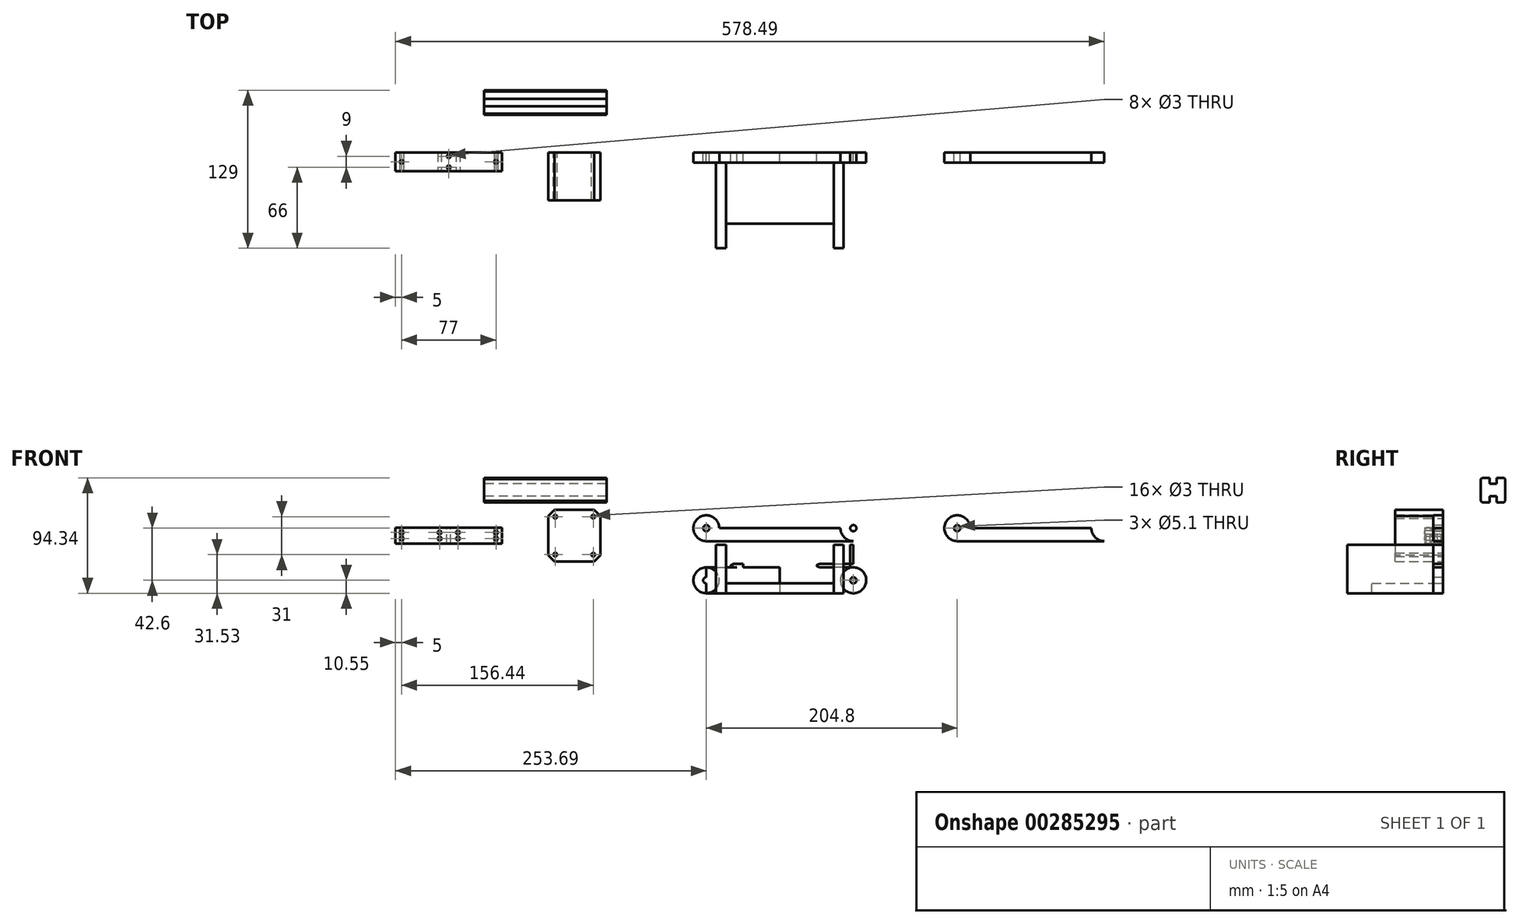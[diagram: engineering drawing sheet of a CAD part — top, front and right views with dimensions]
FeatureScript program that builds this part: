
annotation { "Feature Type Name" : "Feature", "Feature Type Description" : "" }
export const myFeature = defineFeature(function(context is Context, id is Id, definition is map)
    precondition{}
    {
        {
            var Q0;
            Q0=qCreatedBy(makeId("Front.planeOp"),FACE);
            var sketch = newSketch(context, id + "F0", { "sketchPlane" : qUnion([Q0])});
            skLineSegment(sketch, "E0.bottom", {"start": v(-72.24, 27.77) * mm, "end": v(14.76, 27.77) * mm});
            skLineSegment(sketch, "E0.top", {"start": v(-72.24, 14.77) * mm, "end": v(14.76, 14.77) * mm});
            skLineSegment(sketch, "E0.left", {"start": v(-72.24, 27.77) * mm, "end": v(-72.24, 14.77) * mm});
            skLineSegment(sketch, "E0.right", {"start": v(14.76, 27.77) * mm, "end": v(14.76, 14.77) * mm});
            skSolve(sketch);
        }
        {
            var Q0;
            Q0 = qSketchRegion(id + "F0", true);
            extrude(context, id + "F1", {"entities" : qUnion([Q0]), "depth" : 15 * mm, "offsetDistance" : 25 * mm});
        }
        {
            var Q0;
            Q0=makeQuery(id+"F1.opExtrude","CAP_FACE",FACE,{"disambiguationData":[OSD([sQuery(id+"F0.wireOp",EDGE,"E0.bottom"),sQuery(id+"F0.wireOp",EDGE,"E0.top"),sQuery(id+"F0.wireOp",EDGE,"E0.left"),sQuery(id+"F0.wireOp",EDGE,"E0.right")])],"isStart":false});
            var sketch = newSketch(context, id + "F2", { "sketchPlane" : qUnion([Q0])});
            skLineSegment(sketch, "E1.bottom", {"start": v(-72.24, 27.77) * mm, "end": v(14.76, 27.77) * mm});
            skLineSegment(sketch, "E1.top", {"start": v(-72.24, 14.77) * mm, "end": v(14.76, 14.77) * mm});
            skLineSegment(sketch, "E1.left", {"start": v(-72.24, 27.77) * mm, "end": v(-72.24, 14.77) * mm});
            skLineSegment(sketch, "E1.right", {"start": v(14.76, 27.77) * mm, "end": v(14.76, 14.77) * mm});
            skLineSegment(sketch, "E2", {"start": v(-28.74, 27.77) * mm, "end": v(-21.24, 27.77) * mm});
            skLineSegment(sketch, "E3", {"start": v(-21.24, 27.77) * mm, "end": v(-36.24, 27.77) * mm});
            skLineSegment(sketch, "E4", {"start": v(-36.24, 27.77) * mm, "end": v(-67.24, 27.77) * mm});
            skLineSegment(sketch, "E5", {"start": v(-67.24, 27.77) * mm, "end": v(-67.24, 23.77) * mm});
            skLineSegment(sketch, "E6", {"start": v(-67.24, 23.77) * mm, "end": v(-67.24, 18.77) * mm});
            skLineSegment(sketch, "E7", {"start": v(-67.24, 18.77) * mm, "end": v(-67.24, 14.77) * mm});
            skLineSegment(sketch, "E8", {"start": v(-36.24, 27.77) * mm, "end": v(-36.24, 18.77) * mm});
            skLineSegment(sketch, "E9", {"start": v(-36.24, 18.77) * mm, "end": v(-36.24, 23.77) * mm});
            skLineSegment(sketch, "E10", {"start": v(-36.24, 23.77) * mm, "end": v(-21.24, 23.77) * mm});
            skLineSegment(sketch, "E11", {"start": v(-21.24, 23.77) * mm, "end": v(-21.24, 18.77) * mm});
            skLineSegment(sketch, "E12", {"start": v(-21.24, 18.77) * mm, "end": v(9.76, 18.77) * mm});
            skLineSegment(sketch, "E13", {"start": v(9.76, 18.77) * mm, "end": v(9.76, 23.77) * mm});
            skCircle(sketch, "E14", {"center": v(-67.24, 23.77) * mm, "radius": 1.5 * mm});
            skCircle(sketch, "E15", {"center": v(-67.24, 18.77) * mm, "radius": 1.5 * mm});
            skCircle(sketch, "E16", {"center": v(-36.24, 23.77) * mm, "radius": 1.5 * mm});
            skCircle(sketch, "E17", {"center": v(-36.24, 18.77) * mm, "radius": 1.5 * mm});
            skCircle(sketch, "E18", {"center": v(9.76, 23.77) * mm, "radius": 1.5 * mm});
            skCircle(sketch, "E19", {"center": v(9.76, 18.77) * mm, "radius": 1.5 * mm});
            skCircle(sketch, "E20", {"center": v(-21.24, 23.77) * mm, "radius": 1.5 * mm});
            skCircle(sketch, "E21", {"center": v(-21.24, 18.77) * mm, "radius": 1.5 * mm});
            skSolve(sketch);
        }
        {
            var Q0;
            {var subQ0=sQuery(id+"F2.wireOp",EDGE,"E6");var subQ1=sQuery(id+"F2.wireOp",EDGE,"E5");var subQ2=makeQuery(id+"F2.imprint","INTERSECT",VERTEX,{"derivedFrom":[subQ1,subQ0]});Q0=makeQuery(id+"F2.imprint","IMPRINT",FACE,{"disambiguationData":[TD([[makeQuery(id+"F2.imprint","IMPRINT",EDGE,{"disambiguationData":[TD([[subQ2,1.0]])],"derivedFrom":subQ1}),1.0]])]});}
            var Q1;
            {var subQ0=sQuery(id+"F2.wireOp",EDGE,"E6");var subQ1=sQuery(id+"F2.wireOp",EDGE,"E5");var subQ2=makeQuery(id+"F2.imprint","INTERSECT",VERTEX,{"derivedFrom":[subQ1,subQ0]});Q1=makeQuery(id+"F2.imprint","IMPRINT",FACE,{"disambiguationData":[TD([[makeQuery(id+"F2.imprint","IMPRINT",EDGE,{"disambiguationData":[TD([[subQ2,1.0]])],"derivedFrom":subQ1}),-1.0]])]});}
            var Q2;
            {var subQ0=sQuery(id+"F2.wireOp",EDGE,"E7");var subQ1=sQuery(id+"F2.wireOp",EDGE,"E6");var subQ2=makeQuery(id+"F2.imprint","INTERSECT",VERTEX,{"derivedFrom":[subQ1,subQ0]});Q2=makeQuery(id+"F2.imprint","IMPRINT",FACE,{"disambiguationData":[TD([[makeQuery(id+"F2.imprint","IMPRINT",EDGE,{"disambiguationData":[TD([[subQ2,1.0]])],"derivedFrom":subQ1}),-1.0]])]});}
            var Q3;
            {var subQ0=sQuery(id+"F2.wireOp",EDGE,"E7");var subQ1=sQuery(id+"F2.wireOp",EDGE,"E6");var subQ2=makeQuery(id+"F2.imprint","INTERSECT",VERTEX,{"derivedFrom":[subQ1,subQ0]});Q3=makeQuery(id+"F2.imprint","IMPRINT",FACE,{"disambiguationData":[TD([[makeQuery(id+"F2.imprint","IMPRINT",EDGE,{"disambiguationData":[TD([[subQ2,1.0]])],"derivedFrom":subQ1}),1.0]])]});}
            var Q4;
            {var subQ1=sQuery(id+"F2.wireOp",EDGE,"E9");var subQ3=sQuery(id+"F2.wireOp",EDGE,"E16");var subQ4=makeQuery(id+"F2.imprint","INTERSECT",VERTEX,{"derivedFrom":[subQ1,subQ3]});Q4=makeQuery(id+"F2.imprint","IMPRINT",FACE,{"disambiguationData":[TD([[makeQuery(id+"F2.imprint","IMPRINT",EDGE,{"disambiguationData":[TD([[subQ4,-1.0]])],"derivedFrom":subQ3}),1.0]])]});}
            var Q5;
            {var subQ1=sQuery(id+"F2.wireOp",EDGE,"E8");var subQ3=sQuery(id+"F2.wireOp",EDGE,"E16");var subQ4=makeQuery(id+"F2.imprint","INTERSECT",VERTEX,{"derivedFrom":[subQ1,subQ3]});Q5=makeQuery(id+"F2.imprint","IMPRINT",FACE,{"disambiguationData":[TD([[makeQuery(id+"F2.imprint","IMPRINT",EDGE,{"disambiguationData":[TD([[subQ4,-1.0]])],"derivedFrom":subQ3}),1.0]])]});}
            var Q6;
            {var subQ1=sQuery(id+"F2.wireOp",EDGE,"E8");var subQ3=sQuery(id+"F2.wireOp",EDGE,"E16");var subQ4=makeQuery(id+"F2.imprint","INTERSECT",VERTEX,{"derivedFrom":[subQ1,subQ3]});Q6=makeQuery(id+"F2.imprint","IMPRINT",FACE,{"disambiguationData":[TD([[makeQuery(id+"F2.imprint","IMPRINT",EDGE,{"disambiguationData":[TD([[subQ4,1.0]])],"derivedFrom":subQ3}),1.0]])]});}
            var Q7;
            Q7=makeQuery(id+"F2.imprint","IMPRINT",FACE,{"disambiguationData":[TD([[makeQuery(id+"F2.imprint","IMPRINT",EDGE,{"derivedFrom":sQuery(id+"F2.wireOp",EDGE,"E17")}),1.0]])]});
            var Q8;
            {var subQ0=sQuery(id+"F2.wireOp",EDGE,"E11");var subQ1=sQuery(id+"F2.wireOp",EDGE,"E10");var subQ2=makeQuery(id+"F2.imprint","INTERSECT",VERTEX,{"derivedFrom":[subQ1,subQ0]});Q8=makeQuery(id+"F2.imprint","IMPRINT",FACE,{"disambiguationData":[TD([[makeQuery(id+"F2.imprint","IMPRINT",EDGE,{"disambiguationData":[TD([[subQ2,1.0]])],"derivedFrom":subQ1}),1.0]])]});}
            var Q9;
            {var subQ0=sQuery(id+"F2.wireOp",EDGE,"E11");var subQ1=sQuery(id+"F2.wireOp",EDGE,"E10");var subQ2=makeQuery(id+"F2.imprint","INTERSECT",VERTEX,{"derivedFrom":[subQ1,subQ0]});Q9=makeQuery(id+"F2.imprint","IMPRINT",FACE,{"disambiguationData":[TD([[makeQuery(id+"F2.imprint","IMPRINT",EDGE,{"disambiguationData":[TD([[subQ2,1.0]])],"derivedFrom":subQ1}),-1.0]])]});}
            var Q10;
            {var subQ0=sQuery(id+"F2.wireOp",EDGE,"E12");var subQ1=sQuery(id+"F2.wireOp",EDGE,"E11");var subQ2=makeQuery(id+"F2.imprint","INTERSECT",VERTEX,{"derivedFrom":[subQ1,subQ0]});Q10=makeQuery(id+"F2.imprint","IMPRINT",FACE,{"disambiguationData":[TD([[makeQuery(id+"F2.imprint","IMPRINT",EDGE,{"disambiguationData":[TD([[subQ2,1.0]])],"derivedFrom":subQ1}),-1.0]])]});}
            var Q11;
            {var subQ0=sQuery(id+"F2.wireOp",EDGE,"E12");var subQ1=sQuery(id+"F2.wireOp",EDGE,"E11");var subQ2=makeQuery(id+"F2.imprint","INTERSECT",VERTEX,{"derivedFrom":[subQ1,subQ0]});Q11=makeQuery(id+"F2.imprint","IMPRINT",FACE,{"disambiguationData":[TD([[makeQuery(id+"F2.imprint","IMPRINT",EDGE,{"disambiguationData":[TD([[subQ2,1.0]])],"derivedFrom":subQ1}),1.0]])]});}
            var Q12;
            {var subQ0=sQuery(id+"F2.wireOp",EDGE,"E13");var subQ1=sQuery(id+"F2.wireOp",EDGE,"E12");var subQ2=makeQuery(id+"F2.imprint","INTERSECT",VERTEX,{"derivedFrom":[subQ1,subQ0]});Q12=makeQuery(id+"F2.imprint","IMPRINT",FACE,{"disambiguationData":[TD([[makeQuery(id+"F2.imprint","IMPRINT",EDGE,{"disambiguationData":[TD([[subQ2,1.0]])],"derivedFrom":subQ1}),-1.0]])]});}
            var Q13;
            {var subQ0=sQuery(id+"F2.wireOp",EDGE,"E13");var subQ1=sQuery(id+"F2.wireOp",EDGE,"E12");var subQ2=makeQuery(id+"F2.imprint","INTERSECT",VERTEX,{"derivedFrom":[subQ1,subQ0]});Q13=makeQuery(id+"F2.imprint","IMPRINT",FACE,{"disambiguationData":[TD([[makeQuery(id+"F2.imprint","IMPRINT",EDGE,{"disambiguationData":[TD([[subQ2,1.0]])],"derivedFrom":subQ1}),1.0]])]});}
            var Q14;
            Q14=makeQuery(id+"F2.imprint","IMPRINT",FACE,{"disambiguationData":[TD([[makeQuery(id+"F2.imprint","IMPRINT",EDGE,{"derivedFrom":sQuery(id+"F2.wireOp",EDGE,"E18")}),1.0]])]});
            extrude(context, id + "F3", {"entities" : qUnion([Q0, Q1, Q2, Q3, Q4, Q5, Q6, Q7, Q8, Q9, Q10, Q11, Q12, Q13, Q14]), "operationType" : NewBodyOperationType.REMOVE, "oppositeDirection" : true, "depth" : 25 * mm, "offsetDistance" : 25 * mm});
        }
        {
            var Q0;
            Q0=makeQuery(id+"F1.opExtrude","SWEPT_FACE",FACE,{"disambiguationData":[OSD([sQuery(id+"F0.wireOp",EDGE,"E0.bottom")])]});
            var sketch = newSketch(context, id + "F4", { "sketchPlane" : qUnion([Q0])});
            skLineSegment(sketch, "E22", {"start": v(-72.24, -7.5) * mm, "end": v(14.76, -7.5) * mm});
            skLineSegment(sketch, "E23", {"start": v(-28.74, -15) * mm, "end": v(-28.74, 0) * mm});
            skLineSegment(sketch, "E24", {"start": v(-72.24, -7.5) * mm, "end": v(-67.24, -7.5) * mm});
            skLineSegment(sketch, "E25", {"start": v(14.76, -7.5) * mm, "end": v(9.76, -7.5) * mm});
            skLineSegment(sketch, "E26", {"start": v(-28.74, 0) * mm, "end": v(-28.74, -3) * mm});
            skLineSegment(sketch, "E27", {"start": v(-28.74, -3) * mm, "end": v(-28.74, -15) * mm});
            skLineSegment(sketch, "E28", {"start": v(-28.74, -15) * mm, "end": v(-28.74, -12) * mm});
            skCircle(sketch, "E29", {"center": v(-28.74, -12) * mm, "radius": 1.5 * mm});
            skCircle(sketch, "E30", {"center": v(-28.74, -3) * mm, "radius": 1.5 * mm});
            skCircle(sketch, "E31", {"center": v(9.76, -7.5) * mm, "radius": 1.5 * mm});
            skCircle(sketch, "E32", {"center": v(-67.24, -7.5) * mm, "radius": 1.5 * mm});
            skSolve(sketch);
        }
        {
            var Q0;
            Q0 = qSketchRegion(id + "F4", true);
            extrude(context, id + "F5", {"entities" : qUnion([Q0]), "operationType" : NewBodyOperationType.REMOVE, "oppositeDirection" : true, "depth" : 25 * mm, "offsetDistance" : 25 * mm});
        }
        {
            var Q0;
            Q0=qCreatedBy(makeId("Front.planeOp"),FACE);
            var sketch = newSketch(context, id + "F6", { "sketchPlane" : qUnion([Q0])});
            skLineSegment(sketch, "E33.bottom", {"start": v(52.55, 42.3) * mm, "end": v(94.85, 42.3) * mm});
            skLineSegment(sketch, "E33.top", {"start": v(52.55, 0) * mm, "end": v(94.85, 0) * mm});
            skLineSegment(sketch, "E33.left", {"start": v(52.55, 42.3) * mm, "end": v(52.55, 0) * mm});
            skLineSegment(sketch, "E33.right", {"start": v(94.85, 42.3) * mm, "end": v(94.85, 0) * mm});
            skLineSegment(sketch, "E34", {"start": v(58.2, 36.65) * mm, "end": v(89.2, 36.65) * mm});
            skLineSegment(sketch, "E35", {"start": v(89.2, 36.65) * mm, "end": v(94.85, 36.65) * mm});
            skLineSegment(sketch, "E36", {"start": v(58.2, 36.65) * mm, "end": v(52.55, 36.65) * mm});
            skLineSegment(sketch, "E37", {"start": v(58.2, 36.65) * mm, "end": v(58.2, 42.3) * mm});
            skLineSegment(sketch, "E38", {"start": v(58.2, 36.65) * mm, "end": v(58.2, 5.65) * mm});
            skLineSegment(sketch, "E39", {"start": v(58.2, 5.65) * mm, "end": v(89.2, 5.65) * mm});
            skLineSegment(sketch, "E40", {"start": v(89.2, 5.65) * mm, "end": v(89.2, 36.65) * mm});
            skCircle(sketch, "E41", {"center": v(58.2, 36.65) * mm, "radius": 1.5 * mm});
            skCircle(sketch, "E42", {"center": v(89.2, 36.65) * mm, "radius": 1.5 * mm});
            skCircle(sketch, "E43", {"center": v(89.2, 5.65) * mm, "radius": 1.5 * mm});
            skCircle(sketch, "E44", {"center": v(58.2, 5.65) * mm, "radius": 1.5 * mm});
            skSolve(sketch);
        }
        {
            var Q0;
            Q0 = qSketchRegion(id + "F6", true);
            var Q1;
            {var subQ5=sQuery(id+"F6.wireOp",EDGE,"E41");var subQ9=sQuery(id+"F6.wireOp",EDGE,"E34");var subQ10=makeQuery(id+"F6.imprint","INTERSECT",VERTEX,{"derivedFrom":[subQ9,subQ5]});Q1=makeQuery(id+"F6.imprint","IMPRINT",FACE,{"disambiguationData":[TD([[makeQuery(id+"F6.imprint","IMPRINT",EDGE,{"disambiguationData":[TD([[subQ10,-1.0]])],"derivedFrom":subQ9}),-1.0]])]});}
            extrude(context, id + "F7", {"entities" : qUnion([Q0, Q1]), "depth" : 39 * mm, "offsetDistance" : 25 * mm});
        }
        {
            var Q0;
            Q0=makeQuery(id+"F7.opExtrude","SWEPT_EDGE",EDGE,{"disambiguationData":[OSD([sQuery(id+"F6.wireOp",EDGE,"E33.bottom"),sQuery(id+"F6.wireOp",EDGE,"E33.left")])]});
            var Q1;
            Q1=makeQuery(id+"F7.opExtrude","SWEPT_EDGE",EDGE,{"disambiguationData":[OSD([sQuery(id+"F6.wireOp",EDGE,"E33.bottom"),sQuery(id+"F6.wireOp",EDGE,"E33.right")])]});
            var Q2;
            Q2=makeQuery(id+"F7.opExtrude","SWEPT_EDGE",EDGE,{"disambiguationData":[OSD([sQuery(id+"F6.wireOp",EDGE,"E33.top"),sQuery(id+"F6.wireOp",EDGE,"E33.left")])]});
            var Q3;
            Q3=makeQuery(id+"F7.opExtrude","SWEPT_EDGE",EDGE,{"disambiguationData":[OSD([sQuery(id+"F6.wireOp",EDGE,"E33.top"),sQuery(id+"F6.wireOp",EDGE,"E33.right")])]});
            chamfer(context, id + "F8", {"entities" : qUnion([Q0, Q1, Q2, Q3]), "width" : 5 * mm, "tangentPropagation" : true});
        }
        {
            var Q0;
            Q0=qCreatedBy(makeId("Right.planeOp"),FACE);
            var sketch = newSketch(context, id + "F9", { "sketchPlane" : qUnion([Q0])});
            skLineSegment(sketch, "E45.bottom", {"start": v(51, 68.46) * mm, "end": v(31, 68.46) * mm});
            skLineSegment(sketch, "E45.top", {"start": v(51, 48.46) * mm, "end": v(31, 48.46) * mm});
            skLineSegment(sketch, "E45.left", {"start": v(51, 68.46) * mm, "end": v(51, 48.46) * mm});
            skLineSegment(sketch, "E45.right", {"start": v(31, 68.46) * mm, "end": v(31, 48.46) * mm});
            skSolve(sketch);
        }
        {
            var Q0;
            Q0 = qSketchRegion(id + "F9", true);
            extrude(context, id + "F10", {"entities" : qUnion([Q0]), "depth" : 100 * mm, "offsetDistance" : 25 * mm});
        }
        {
            var Q0;
            Q0=makeQuery(id+"F10.opExtrude","SWEPT_EDGE",EDGE,{"disambiguationData":[OSD([sQuery(id+"F9.wireOp",EDGE,"E45.bottom"),sQuery(id+"F9.wireOp",EDGE,"E45.right")])]});
            var Q1;
            Q1=makeQuery(id+"F10.opExtrude","SWEPT_EDGE",EDGE,{"disambiguationData":[OSD([sQuery(id+"F9.wireOp",EDGE,"E45.bottom"),sQuery(id+"F9.wireOp",EDGE,"E45.left")])]});
            var Q2;
            Q2=makeQuery(id+"F10.opExtrude","SWEPT_EDGE",EDGE,{"disambiguationData":[OSD([sQuery(id+"F9.wireOp",EDGE,"E45.top"),sQuery(id+"F9.wireOp",EDGE,"E45.right")])]});
            var Q3;
            Q3=makeQuery(id+"F10.opExtrude","SWEPT_EDGE",EDGE,{"disambiguationData":[OSD([sQuery(id+"F9.wireOp",EDGE,"E45.top"),sQuery(id+"F9.wireOp",EDGE,"E45.left")])]});
            chamfer(context, id + "F11", {"entities" : qUnion([Q0, Q1, Q2, Q3]), "width" : 1 * mm, "tangentPropagation" : true});
        }
        {
            var Q0;
            Q0=makeQuery(id+"F10.opExtrude","CAP_FACE",FACE,{"disambiguationData":[OSD([sQuery(id+"F9.wireOp",EDGE,"E45.bottom"),sQuery(id+"F9.wireOp",EDGE,"E45.top"),sQuery(id+"F9.wireOp",EDGE,"E45.left"),sQuery(id+"F9.wireOp",EDGE,"E45.right")])],"isStart":true});
            var sketch = newSketch(context, id + "F12", { "sketchPlane" : qUnion([Q0])});
            skLineSegment(sketch, "E46.bottom", {"start": v(-51, 68.46) * mm, "end": v(-31, 68.46) * mm});
            skLineSegment(sketch, "E46.top", {"start": v(-51, 48.46) * mm, "end": v(-31, 48.46) * mm});
            skLineSegment(sketch, "E46.left", {"start": v(-51, 68.46) * mm, "end": v(-51, 48.46) * mm});
            skLineSegment(sketch, "E46.right", {"start": v(-31, 68.46) * mm, "end": v(-31, 48.46) * mm});
            skLineSegment(sketch, "E47", {"start": v(-41, 68.46) * mm, "end": v(-41, 48.46) * mm});
            skLineSegment(sketch, "E48", {"start": v(-51, 58.46) * mm, "end": v(-51, 61.46) * mm});
            skLineSegment(sketch, "E49", {"start": v(-51, 61.46) * mm, "end": v(-51, 55.46) * mm});
            skLineSegment(sketch, "E50", {"start": v(-51, 55.46) * mm, "end": v(-31, 55.46) * mm});
            skLineSegment(sketch, "E51", {"start": v(-31, 55.46) * mm, "end": v(-31, 61.46) * mm});
            skLineSegment(sketch, "E52", {"start": v(-31, 61.46) * mm, "end": v(-51, 61.46) * mm});
            skLineSegment(sketch, "E53", {"start": v(-51, 61.46) * mm, "end": v(-46, 61.46) * mm});
            skLineSegment(sketch, "E54", {"start": v(-46, 61.46) * mm, "end": v(-46, 55.46) * mm});
            skLineSegment(sketch, "E55", {"start": v(-41, 68.46) * mm, "end": v(-38, 68.46) * mm});
            skLineSegment(sketch, "E56", {"start": v(-38, 68.46) * mm, "end": v(-44, 68.46) * mm});
            skLineSegment(sketch, "E57", {"start": v(-44, 68.46) * mm, "end": v(-44, 63.46) * mm});
            skLineSegment(sketch, "E58", {"start": v(-38, 68.46) * mm, "end": v(-38, 63.46) * mm});
            skLineSegment(sketch, "E59", {"start": v(-38, 63.46) * mm, "end": v(-44, 63.46) * mm});
            skLineSegment(sketch, "E60.MirrorCS", {"start": v(-36, 61.46) * mm, "end": v(-36, 55.46) * mm});
            skLineSegment(sketch, "E61", {"start": v(-41, 58.46) * mm, "end": v(-36, 58.46) * mm});
            skLineSegment(sketch, "E62.MirrorCS", {"start": v(-38, 53.46) * mm, "end": v(-44, 53.46) * mm});
            skLineSegment(sketch, "E63.MirrorCS", {"start": v(-38, 48.46) * mm, "end": v(-38, 53.46) * mm});
            skLineSegment(sketch, "E64.MirrorCS", {"start": v(-44, 48.46) * mm, "end": v(-44, 53.46) * mm});
            skSolve(sketch);
        }
        {
            var Q0;
            {var subQ3=sQuery(id+"F12.wireOp",EDGE,"E64.MirrorCS");Q0=makeQuery(id+"F12.imprint","IMPRINT",FACE,{"disambiguationData":[TD([[makeQuery(id+"F12.imprint","IMPRINT",EDGE,{"derivedFrom":subQ3}),-1.0]])]});}
            var Q1;
            {var subQ3=sQuery(id+"F12.wireOp",EDGE,"E63.MirrorCS");Q1=makeQuery(id+"F12.imprint","IMPRINT",FACE,{"disambiguationData":[TD([[makeQuery(id+"F12.imprint","IMPRINT",EDGE,{"derivedFrom":subQ3}),1.0]])]});}
            var Q2;
            {var subQ5=sQuery(id+"F12.wireOp",EDGE,"E57");Q2=makeQuery(id+"F12.imprint","IMPRINT",FACE,{"disambiguationData":[TD([[makeQuery(id+"F12.imprint","IMPRINT",EDGE,{"derivedFrom":subQ5}),1.0]])]});}
            var Q3;
            {var subQ5=sQuery(id+"F12.wireOp",EDGE,"E58");Q3=makeQuery(id+"F12.imprint","IMPRINT",FACE,{"disambiguationData":[TD([[makeQuery(id+"F12.imprint","IMPRINT",EDGE,{"derivedFrom":subQ5}),-1.0]])]});}
            var Q4;
            {var subQ0=sQuery(id+"F12.wireOp",EDGE,"E53");Q4=makeQuery(id+"F12.imprint","IMPRINT",FACE,{"disambiguationData":[TD([[makeQuery(id+"F12.imprint","IMPRINT",EDGE,{"derivedFrom":subQ0}),-1.0]])]});}
            var Q5;
            {var subQ4=sQuery(id+"F12.wireOp",EDGE,"E51");Q5=makeQuery(id+"F12.imprint","IMPRINT",FACE,{"disambiguationData":[TD([[makeQuery(id+"F12.imprint","IMPRINT",EDGE,{"derivedFrom":subQ4}),-1.0]])]});}
            extrude(context, id + "F13", {"entities" : qUnion([Q0, Q1, Q2, Q3, Q4, Q5]), "operationType" : NewBodyOperationType.REMOVE, "oppositeDirection" : true, "depth" : 148.2 * mm, "offsetDistance" : 25 * mm});
        }
        {
            var Q0;
            Q0=qCreatedBy(makeId("Front.planeOp"),FACE);
            var sketch = newSketch(context, id + "F14", { "sketchPlane" : qUnion([Q0])});
            skLineSegment(sketch, "E65.bottom", {"start": v(181.45, 27.27) * mm, "end": v(290.9, 27.27) * mm});
            skLineSegment(sketch, "E65.top", {"start": v(181.45, -15.33) * mm, "end": v(290.9, -15.33) * mm});
            skLineSegment(sketch, "E65.left", {"start": v(181.45, 27.27) * mm, "end": v(181.45, -15.33) * mm});
            skCircle(sketch, "E66", {"center": v(181.45, 27.27) * mm, "radius": 2.55 * mm});
            skCircle(sketch, "E67", {"center": v(181.45, -15.33) * mm, "radius": 2.55 * mm});
            skCircle(sketch, "E68.0", {"center": v(181.45, 27.27) * mm, "radius": 10.55 * mm});
            skCircle(sketch, "E69.0", {"center": v(181.45, -15.33) * mm, "radius": 10.55 * mm});
            skLineSegment(sketch, "E70", {"start": v(178.9, 27.27) * mm, "end": v(170.9, 27.27) * mm});
            skLineSegment(sketch, "E71", {"start": v(181.45, -15.33) * mm, "end": v(170.9, -15.33) * mm});
            skLineSegment(sketch, "E72.left", {"start": v(181.45, -4.78) * mm, "end": v(181.45, 16.72) * mm});
            skLineSegment(sketch, "E73", {"start": v(181.45, 16.72) * mm, "end": v(290.9, 16.72) * mm});
            skLineSegment(sketch, "E74", {"start": v(181.45, 13.72) * mm, "end": v(290.9, 13.72) * mm});
            skLineSegment(sketch, "E75", {"start": v(181.45, -4.78) * mm, "end": v(262.83, -4.78) * mm});
            skLineSegment(sketch, "E76", {"start": v(181.45, -4.78) * mm, "end": v(181.45, -1.78) * mm});
            skLineSegment(sketch, "E77", {"start": v(181.45, -1.78) * mm, "end": v(290.9, -1.78) * mm});
            skLineSegment(sketch, "E78", {"start": v(241.45, 27.27) * mm, "end": v(241.45, -15.33) * mm});
            skLineSegment(sketch, "E79", {"start": v(290.9, -15.33) * mm, "end": v(301.45, -15.33) * mm});
            skCircle(sketch, "E80", {"center": v(301.45, -15.33) * mm, "radius": 10.55 * mm});
            skCircle(sketch, "E81", {"center": v(301.45, -15.33) * mm, "radius": 2.55 * mm});
            skCircle(sketch, "E82.MirrorC", {"center": v(301.45, 27.27) * mm, "radius": 10.55 * mm});
            skCircle(sketch, "E83.MirrorC", {"center": v(301.45, 27.27) * mm, "radius": 2.55 * mm});
            skLineSegment(sketch, "E84.MirrorCS", {"start": v(282.73, 27.27) * mm, "end": v(293.28, 27.27) * mm});
            skLineSegment(sketch, "E85.top", {"start": v(192, -15.33) * mm, "end": v(184, -15.33) * mm});
            skLineSegment(sketch, "E86.top", {"start": v(282.73, -15.33) * mm, "end": v(290.73, -15.33) * mm});
            skLineSegment(sketch, "E87", {"start": v(301.45, 27.27) * mm, "end": v(301.45, -15.33) * mm});
            skLineSegment(sketch, "E88", {"start": v(290.9, 13.72) * mm, "end": v(301.45, 13.72) * mm});
            skLineSegment(sketch, "E89", {"start": v(301.45, 13.72) * mm, "end": v(301.45, 16.72) * mm});
            skLineSegment(sketch, "E90", {"start": v(301.45, 16.72) * mm, "end": v(290.9, 16.72) * mm});
            skLineSegment(sketch, "E91", {"start": v(290.9, -1.78) * mm, "end": v(301.45, -1.78) * mm});
            skLineSegment(sketch, "E92", {"start": v(301.45, -1.78) * mm, "end": v(301.45, -4.78) * mm});
            skLineSegment(sketch, "E93", {"start": v(301.45, -4.78) * mm, "end": v(262.83, -4.78) * mm});
            skLineSegment(sketch, "E94", {"start": v(241.45, 16.72) * mm, "end": v(241.45, 13.72) * mm});
            skLineSegment(sketch, "E95", {"start": v(241.45, 13.72) * mm, "end": v(241.45, -1.78) * mm});
            skLineSegment(sketch, "E96", {"start": v(241.45, -1.78) * mm, "end": v(241.45, -4.78) * mm});
            skLineSegment(sketch, "E97", {"start": v(241.45, -4.78) * mm, "end": v(181.45, -4.78) * mm});
            skLineSegment(sketch, "E98", {"start": v(211.45, -4.78) * mm, "end": v(211.45, 16.72) * mm});
            skLineSegment(sketch, "E99", {"start": v(211.45, 16.72) * mm, "end": v(211.45, 13.72) * mm});
            skLineSegment(sketch, "E100", {"start": v(211.45, 13.72) * mm, "end": v(211.45, 15.22) * mm});
            skLineSegment(sketch, "E101", {"start": v(211.45, 15.22) * mm, "end": v(206.45, 15.22) * mm});
            skLineSegment(sketch, "E102", {"start": v(206.45, 15.22) * mm, "end": v(206.45, 16.72) * mm});
            skEllipse(sketch, "E103", {"center": v(206.45, 15.22) * mm, "majorRadius": 5 * mm, "minorRadius": 1.5 * mm, "majorAxis": v(1, 0)});
            skLineSegment(sketch, "E104", {"start": v(241.45, 5.97) * mm, "end": v(235.44, 5.97) * mm});
            skEllipse(sketch, "E105.MirrorC", {"center": v(206.45, -3.28) * mm, "majorRadius": 5 * mm, "minorRadius": 1.5 * mm, "majorAxis": v(1, 0)});
            skEllipse(sketch, "E106.MirrorC", {"center": v(276.45, 15.22) * mm, "majorRadius": 5 * mm, "minorRadius": 1.5 * mm, "majorAxis": v(-1, 0)});
            skEllipse(sketch, "E107.MirrorC", {"center": v(276.45, -3.28) * mm, "majorRadius": 5 * mm, "minorRadius": 1.5 * mm, "majorAxis": v(-1, 0)});
            skLineSegment(sketch, "E108", {"start": v(181.45, -15.33) * mm, "end": v(181.45, -25.88) * mm});
            skLineSegment(sketch, "E109", {"start": v(181.45, -25.88) * mm, "end": v(301.45, -25.88) * mm});
            skLineSegment(sketch, "E110", {"start": v(192, -25.88) * mm, "end": v(290.9, -25.88) * mm});
            skLineSegment(sketch, "E111", {"start": v(192, 13.72) * mm, "end": v(184, 13.72) * mm});
            skLineSegment(sketch, "E112", {"start": v(290.9, 13.72) * mm, "end": v(298.9, 13.72) * mm});
            skLineSegment(sketch, "E113", {"start": v(298.9, 13.72) * mm, "end": v(298.9, -25.57) * mm});
            skLineSegment(sketch, "E114", {"start": v(241.45, -15.33) * mm, "end": v(241.45, -25.88) * mm});
            skLineSegment(sketch, "E115", {"start": v(241.45, -25.88) * mm, "end": v(285.45, -25.88) * mm});
            skSolve(sketch);
        }
        {
            var Q0;
            Q0=makeQuery(id+"F14.imprint","IMPRINT",FACE,{"disambiguationData":[TD([[makeQuery(id+"F14.imprint","IMPRINT",EDGE,{"derivedFrom":sQuery(id+"F14.wireOp",EDGE,"E83.MirrorC")}),1.0]])]});
            var Q1;
            {var subQ5=sQuery(id+"F14.wireOp",EDGE,"E70");Q1=makeQuery(id+"F14.imprint","IMPRINT",FACE,{"disambiguationData":[TD([[makeQuery(id+"F14.imprint","IMPRINT",EDGE,{"derivedFrom":subQ5}),-1.0]])]});}
            var Q2;
            {var subQ3=sQuery(id+"F14.wireOp",EDGE,"E114");Q2=makeQuery(id+"F14.imprint","IMPRINT",FACE,{"disambiguationData":[TD([[makeQuery(id+"F14.imprint","IMPRINT",EDGE,{"derivedFrom":subQ3}),-1.0]])]});}
            var Q3;
            {var subQ5=sQuery(id+"F14.wireOp",EDGE,"E70");Q3=makeQuery(id+"F14.imprint","IMPRINT",FACE,{"disambiguationData":[TD([[makeQuery(id+"F14.imprint","IMPRINT",EDGE,{"derivedFrom":subQ5}),1.0]])]});}
            var Q4;
            {var subQ1=sQuery(id+"F14.wireOp",EDGE,"E65.left");var subQ3=sQuery(id+"F14.wireOp",EDGE,"E67");var subQ4=makeQuery(id+"F14.imprint","INTERSECT",VERTEX,{"derivedFrom":[subQ1,subQ3]});Q4=makeQuery(id+"F14.imprint","IMPRINT",FACE,{"disambiguationData":[TD([[makeQuery(id+"F14.imprint","IMPRINT",EDGE,{"disambiguationData":[TD([[subQ4,-1.0]])],"derivedFrom":subQ3}),-1.0]])]});}
            var Q5;
            {var subQ0=sQuery(id+"F14.wireOp",EDGE,"E71");var subQ1=sQuery(id+"F14.wireOp",EDGE,"E67");var subQ2=makeQuery(id+"F14.imprint","INTERSECT",VERTEX,{"derivedFrom":[subQ1,subQ0]});Q5=makeQuery(id+"F14.imprint","IMPRINT",FACE,{"disambiguationData":[TD([[makeQuery(id+"F14.imprint","IMPRINT",EDGE,{"disambiguationData":[TD([[subQ2,-1.0]])],"derivedFrom":subQ1}),-1.0]])]});}
            var Q6;
            {var subQ0=sQuery(id+"F14.wireOp",EDGE,"E76");Q6=makeQuery(id+"F14.imprint","IMPRINT",FACE,{"disambiguationData":[TD([[makeQuery(id+"F14.imprint","IMPRINT",EDGE,{"derivedFrom":subQ0}),-1.0]])]});}
            var Q7;
            {var subQ1=sQuery(id+"F14.wireOp",EDGE,"E80");var subQ3=sQuery(id+"F14.wireOp",EDGE,"E113");var subQ4=makeQuery(id+"F14.imprint","INTERSECT",VERTEX,{"disambiguationData":[OD(1.0)],"derivedFrom":[subQ1,subQ3]});Q7=makeQuery(id+"F14.imprint","IMPRINT",FACE,{"disambiguationData":[TD([[makeQuery(id+"F14.imprint","IMPRINT",EDGE,{"disambiguationData":[TD([[subQ4,1.0]])],"derivedFrom":subQ3}),1.0]])]});}
            var Q8;
            {var subQ0=sQuery(id+"F14.wireOp",EDGE,"E92");Q8=makeQuery(id+"F14.imprint","IMPRINT",FACE,{"disambiguationData":[TD([[makeQuery(id+"F14.imprint","IMPRINT",EDGE,{"derivedFrom":subQ0}),-1.0]])]});}
            var Q9;
            {var subQ0=sQuery(id+"F14.wireOp",EDGE,"E68.0");var subQ1=sQuery(id+"F14.wireOp",EDGE,"E65.bottom");var subQ2=makeQuery(id+"F14.imprint","INTERSECT",VERTEX,{"derivedFrom":[subQ1,subQ0]});Q9=makeQuery(id+"F14.imprint","IMPRINT",FACE,{"disambiguationData":[TD([[makeQuery(id+"F14.imprint","IMPRINT",EDGE,{"disambiguationData":[TD([[subQ2,1.0]])],"derivedFrom":subQ1}),-1.0]])]});}
            var Q10;
            {var subQ0=sQuery(id+"F14.wireOp",EDGE,"E90");Q10=makeQuery(id+"F14.imprint","IMPRINT",FACE,{"disambiguationData":[TD([[makeQuery(id+"F14.imprint","IMPRINT",EDGE,{"derivedFrom":subQ0}),-1.0]])]});}
            var Q11;
            {var subQ4=sQuery(id+"F14.wireOp",EDGE,"E86.top");Q11=makeQuery(id+"F14.imprint","IMPRINT",FACE,{"disambiguationData":[TD([[makeQuery(id+"F14.imprint","IMPRINT",EDGE,{"derivedFrom":subQ4}),-1.0]])]});}
            var Q12;
            {var subQ5=sQuery(id+"F14.wireOp",EDGE,"E85.top");Q12=makeQuery(id+"F14.imprint","IMPRINT",FACE,{"disambiguationData":[TD([[makeQuery(id+"F14.imprint","IMPRINT",EDGE,{"derivedFrom":subQ5}),-1.0]])]});}
            var Q13;
            {var subQ0=sQuery(id+"F14.wireOp",EDGE,"E85.top");Q13=makeQuery(id+"F14.imprint","IMPRINT",FACE,{"disambiguationData":[TD([[makeQuery(id+"F14.imprint","IMPRINT",EDGE,{"derivedFrom":subQ0}),1.0]])]});}
            var Q14;
            {var subQ0=sQuery(id+"F14.wireOp",EDGE,"E87");var subQ5=sQuery(id+"F14.wireOp",EDGE,"E81");var subQ6=makeQuery(id+"F14.imprint","INTERSECT",VERTEX,{"derivedFrom":[subQ5,subQ0]});Q14=makeQuery(id+"F14.imprint","IMPRINT",FACE,{"disambiguationData":[TD([[makeQuery(id+"F14.imprint","IMPRINT",EDGE,{"disambiguationData":[TD([[subQ6,-1.0]])],"derivedFrom":subQ5}),-1.0]])]});}
            var Q15;
            {var subQ5=sQuery(id+"F14.wireOp",EDGE,"E80");var subQ8=makeQuery(id+"F14.imprint","INTERSECT",VERTEX,{"derivedFrom":[subQ5,sQuery(id+"F14.wireOp",EDGE,"E109")]});Q15=makeQuery(id+"F14.imprint","IMPRINT",FACE,{"disambiguationData":[TD([[makeQuery(id+"F14.imprint","IMPRINT",EDGE,{"disambiguationData":[TD([[subQ8,1.0]])],"derivedFrom":subQ5}),1.0]])]});}
            var Q16;
            {var subQ4=sQuery(id+"F14.wireOp",EDGE,"E65.bottom");var subQ7=sQuery(id+"F14.wireOp",EDGE,"E78");var subQ8=makeQuery(id+"F14.imprint","INTERSECT",VERTEX,{"derivedFrom":[subQ4,subQ7]});Q16=makeQuery(id+"F14.imprint","IMPRINT",FACE,{"disambiguationData":[TD([[makeQuery(id+"F14.imprint","IMPRINT",EDGE,{"disambiguationData":[TD([[subQ8,1.0]])],"derivedFrom":subQ4}),-1.0]])]});}
            var Q17;
            {var subQ4=sQuery(id+"F14.wireOp",EDGE,"E111");Q17=makeQuery(id+"F14.imprint","IMPRINT",FACE,{"disambiguationData":[TD([[makeQuery(id+"F14.imprint","IMPRINT",EDGE,{"derivedFrom":subQ4}),1.0]])]});}
            var Q18;
            {var subQ0=sQuery(id+"F14.wireOp",EDGE,"E97");var subQ3=makeQuery(id+"F14.imprint","INTERSECT",VERTEX,{"derivedFrom":[subQ0,sQuery(id+"F14.wireOp",EDGE,"E98")]});Q18=makeQuery(id+"F14.imprint","IMPRINT",FACE,{"disambiguationData":[TD([[makeQuery(id+"F14.imprint","IMPRINT",EDGE,{"disambiguationData":[TD([[subQ3,-1.0]])],"derivedFrom":subQ0}),1.0]])]});}
            var Q19;
            {var subQ7=sQuery(id+"F14.wireOp",EDGE,"E112");Q19=makeQuery(id+"F14.imprint","IMPRINT",FACE,{"disambiguationData":[TD([[makeQuery(id+"F14.imprint","IMPRINT",EDGE,{"derivedFrom":subQ7}),-1.0]])]});}
            var Q20;
            {var subQ0=sQuery(id+"F14.wireOp",EDGE,"E95");var subQ3=makeQuery(id+"F14.imprint","IMPRINT",VERTEX,{"derivedFrom":subQ0});Q20=makeQuery(id+"F14.imprint","IMPRINT",FACE,{"disambiguationData":[TD([[makeQuery(id+"F14.imprint","IMPRINT",EDGE,{"disambiguationData":[TD([[subQ3,1.0]])],"derivedFrom":subQ0}),-1.0]])]});}
            var Q21;
            {var subQ4=sQuery(id+"F14.wireOp",EDGE,"E96");Q21=makeQuery(id+"F14.imprint","IMPRINT",FACE,{"disambiguationData":[TD([[makeQuery(id+"F14.imprint","IMPRINT",EDGE,{"derivedFrom":subQ4}),-1.0]])]});}
            var Q22;
            {var subQ0=sQuery(id+"F14.wireOp",EDGE,"E105.MirrorC");var subQ1=makeQuery(id+"F14.imprint","INTERSECT",VERTEX,{"derivedFrom":[sQuery(id+"F14.wireOp",EDGE,"E77"),subQ0]});Q22=makeQuery(id+"F14.imprint","IMPRINT",FACE,{"disambiguationData":[TD([[makeQuery(id+"F14.imprint","IMPRINT",EDGE,{"disambiguationData":[TD([[subQ1,1.0]])],"derivedFrom":subQ0}),1.0]])]});}
            var Q23;
            {var subQ2=sQuery(id+"F14.wireOp",EDGE,"E75");Q23=makeQuery(id+"F14.imprint","IMPRINT",FACE,{"disambiguationData":[TD([[makeQuery(id+"F14.imprint","IMPRINT",EDGE,{"derivedFrom":subQ2}),1.0]])]});}
            var Q24;
            {var subQ1=sQuery(id+"F14.wireOp",EDGE,"E77");var subQ6=sQuery(id+"F14.wireOp",EDGE,"E91");var subQ9=makeQuery(id+"F14.imprint","INTERSECT",VERTEX,{"derivedFrom":[subQ1,subQ6]});Q24=makeQuery(id+"F14.imprint","IMPRINT",FACE,{"disambiguationData":[TD([[makeQuery(id+"F14.imprint","IMPRINT",EDGE,{"disambiguationData":[TD([[subQ9,1.0]])],"derivedFrom":subQ1}),-1.0]])]});}
            var Q25;
            {var subQ0=sQuery(id+"F14.wireOp",EDGE,"E107.MirrorC");var subQ1=makeQuery(id+"F14.imprint","INTERSECT",VERTEX,{"derivedFrom":[sQuery(id+"F14.wireOp",EDGE,"E77"),subQ0]});Q25=makeQuery(id+"F14.imprint","IMPRINT",FACE,{"disambiguationData":[TD([[makeQuery(id+"F14.imprint","IMPRINT",EDGE,{"disambiguationData":[TD([[subQ1,1.0]])],"derivedFrom":subQ0}),1.0]])]});}
            var Q26;
            {var subQ1=sQuery(id+"F14.wireOp",EDGE,"E75");Q26=makeQuery(id+"F14.imprint","IMPRINT",FACE,{"disambiguationData":[TD([[makeQuery(id+"F14.imprint","IMPRINT",EDGE,{"derivedFrom":subQ1}),-1.0]])]});}
            var Q27;
            {var subQ0=sQuery(id+"F14.wireOp",EDGE,"E80");var subQ3=sQuery(id+"F14.wireOp",EDGE,"E113");var subQ5=makeQuery(id+"F14.imprint","INTERSECT",VERTEX,{"disambiguationData":[OD(1.0)],"derivedFrom":[subQ0,subQ3]});Q27=makeQuery(id+"F14.imprint","IMPRINT",FACE,{"disambiguationData":[TD([[makeQuery(id+"F14.imprint","IMPRINT",EDGE,{"disambiguationData":[TD([[subQ5,-1.0]])],"derivedFrom":subQ0}),1.0]])]});}
            var Q28;
            {var subQ0=sQuery(id+"F14.wireOp",EDGE,"E80");var subQ3=sQuery(id+"F14.wireOp",EDGE,"E113");var subQ5=makeQuery(id+"F14.imprint","INTERSECT",VERTEX,{"disambiguationData":[OD(0.0)],"derivedFrom":[subQ0,subQ3]});Q28=makeQuery(id+"F14.imprint","IMPRINT",FACE,{"disambiguationData":[TD([[makeQuery(id+"F14.imprint","IMPRINT",EDGE,{"disambiguationData":[TD([[subQ5,1.0]])],"derivedFrom":subQ0}),1.0]])]});}
            var Q29;
            {var subQ0=sQuery(id+"F14.wireOp",EDGE,"E94");Q29=makeQuery(id+"F14.imprint","IMPRINT",FACE,{"disambiguationData":[TD([[makeQuery(id+"F14.imprint","IMPRINT",EDGE,{"derivedFrom":subQ0}),-1.0]])]});}
            var Q30;
            {var subQ0=sQuery(id+"F14.wireOp",EDGE,"E94");Q30=makeQuery(id+"F14.imprint","IMPRINT",FACE,{"disambiguationData":[TD([[makeQuery(id+"F14.imprint","IMPRINT",EDGE,{"derivedFrom":subQ0}),1.0]])]});}
            var Q31;
            {var subQ0=sQuery(id+"F14.wireOp",EDGE,"E105.MirrorC");var subQ1=sQuery(id+"F14.wireOp",EDGE,"E77");var subQ2=makeQuery(id+"F14.imprint","INTERSECT",VERTEX,{"derivedFrom":[subQ1,subQ0]});Q31=makeQuery(id+"F14.imprint","IMPRINT",FACE,{"disambiguationData":[TD([[makeQuery(id+"F14.imprint","IMPRINT",EDGE,{"disambiguationData":[TD([[subQ2,-1.0]])],"derivedFrom":subQ1}),-1.0]])]});}
            var Q32;
            {var subQ0=sQuery(id+"F14.wireOp",EDGE,"E98");var subQ1=sQuery(id+"F14.wireOp",EDGE,"E97");var subQ2=makeQuery(id+"F14.imprint","INTERSECT",VERTEX,{"derivedFrom":[subQ1,subQ0]});Q32=makeQuery(id+"F14.imprint","IMPRINT",FACE,{"disambiguationData":[TD([[makeQuery(id+"F14.imprint","IMPRINT",EDGE,{"disambiguationData":[TD([[subQ2,-1.0]])],"derivedFrom":subQ1}),-1.0]])]});}
            var Q33;
            {var subQ0=sQuery(id+"F14.wireOp",EDGE,"E99");Q33=makeQuery(id+"F14.imprint","IMPRINT",FACE,{"disambiguationData":[TD([[makeQuery(id+"F14.imprint","IMPRINT",EDGE,{"derivedFrom":subQ0}),-1.0]])]});}
            var Q34;
            {var subQ0=sQuery(id+"F14.wireOp",EDGE,"E100");Q34=makeQuery(id+"F14.imprint","IMPRINT",FACE,{"disambiguationData":[TD([[makeQuery(id+"F14.imprint","IMPRINT",EDGE,{"derivedFrom":subQ0}),1.0]])]});}
            var Q35;
            {var subQ0=sQuery(id+"F14.wireOp",EDGE,"E88");Q35=makeQuery(id+"F14.imprint","IMPRINT",FACE,{"disambiguationData":[TD([[makeQuery(id+"F14.imprint","IMPRINT",EDGE,{"derivedFrom":subQ0}),-1.0]])]});}
            extrude(context, id + "F15", {"entities" : qUnion([Q0, Q1, Q2, Q3, Q4, Q5, Q6, Q7, Q8, Q9, Q10, Q11, Q12, Q13, Q14, Q15, Q16, Q17, Q18, Q19, Q20, Q21, Q22, Q23, Q24, Q25, Q26, Q27, Q28, Q29, Q30, Q31, Q32, Q33, Q34, Q35]), "depth" : 8 * mm, "offsetDistance" : 25 * mm});
        }
        {
            var Q0;
            Q0=makeQuery(id+"F15.opExtrude","SWEPT_BODY",BODY,{"disambiguationData":[OSD([sQuery(id+"F14.wireOp",EDGE,"E65.bottom"),sQuery(id+"F14.wireOp",EDGE,"E66"),sQuery(id+"F14.wireOp",EDGE,"E67"),sQuery(id+"F14.wireOp",EDGE,"E68.0"),sQuery(id+"F14.wireOp",EDGE,"E69.0"),sQuery(id+"F14.wireOp",EDGE,"E72.left"),sQuery(id+"F14.wireOp",EDGE,"E73"),sQuery(id+"F14.wireOp",EDGE,"E74"),sQuery(id+"F14.wireOp",EDGE,"E76"),sQuery(id+"F14.wireOp",EDGE,"E80"),sQuery(id+"F14.wireOp",EDGE,"E81"),sQuery(id+"F14.wireOp",EDGE,"E82.MirrorC"),sQuery(id+"F14.wireOp",EDGE,"E83.MirrorC"),sQuery(id+"F14.wireOp",EDGE,"E84.MirrorCS"),sQuery(id+"F14.wireOp",EDGE,"E87"),sQuery(id+"F14.wireOp",EDGE,"E88"),sQuery(id+"F14.wireOp",EDGE,"E90"),sQuery(id+"F14.wireOp",EDGE,"E92"),sQuery(id+"F14.wireOp",EDGE,"E103"),sQuery(id+"F14.wireOp",EDGE,"E106.MirrorC"),sQuery(id+"F14.wireOp",EDGE,"E109"),sQuery(id+"F14.wireOp",EDGE,"E110"),sQuery(id+"F14.wireOp",EDGE,"E111"),sQuery(id+"F14.wireOp",EDGE,"E112"),sQuery(id+"F14.wireOp",EDGE,"E115")])]});
            transform(context, id + "F16", {"entities" : qUnion([Q0]), "transformType" : TransformType.TRANSLATION_3D, "dx" : 204.8 * mm, "dy" : 0 * mm, "dz" : 0 * mm, "makeCopy" : true});
        }
        {
            var Q0;
            Q0=makeQuery(id+"F15.opExtrude","CAP_FACE",FACE,{"disambiguationData":[OSD([sQuery(id+"F14.wireOp",EDGE,"E65.bottom"),sQuery(id+"F14.wireOp",EDGE,"E66"),sQuery(id+"F14.wireOp",EDGE,"E67"),sQuery(id+"F14.wireOp",EDGE,"E68.0"),sQuery(id+"F14.wireOp",EDGE,"E69.0"),sQuery(id+"F14.wireOp",EDGE,"E72.left"),sQuery(id+"F14.wireOp",EDGE,"E73"),sQuery(id+"F14.wireOp",EDGE,"E74"),sQuery(id+"F14.wireOp",EDGE,"E76"),sQuery(id+"F14.wireOp",EDGE,"E80"),sQuery(id+"F14.wireOp",EDGE,"E81"),sQuery(id+"F14.wireOp",EDGE,"E82.MirrorC"),sQuery(id+"F14.wireOp",EDGE,"E83.MirrorC"),sQuery(id+"F14.wireOp",EDGE,"E84.MirrorCS"),sQuery(id+"F14.wireOp",EDGE,"E87"),sQuery(id+"F14.wireOp",EDGE,"E88"),sQuery(id+"F14.wireOp",EDGE,"E90"),sQuery(id+"F14.wireOp",EDGE,"E92"),sQuery(id+"F14.wireOp",EDGE,"E103"),sQuery(id+"F14.wireOp",EDGE,"E106.MirrorC"),sQuery(id+"F14.wireOp",EDGE,"E109"),sQuery(id+"F14.wireOp",EDGE,"E110"),sQuery(id+"F14.wireOp",EDGE,"E111"),sQuery(id+"F14.wireOp",EDGE,"E112"),sQuery(id+"F14.wireOp",EDGE,"E115")])],"isStart":false});
            var sketch = newSketch(context, id + "F17", { "sketchPlane" : qUnion([Q0])});
            skLineSegment(sketch, "E116", {"start": v(181.45, -25.88) * mm, "end": v(301.45, -25.88) * mm});
            skLineSegment(sketch, "E117", {"start": v(301.45, -25.88) * mm, "end": v(241.45, -25.88) * mm});
            skLineSegment(sketch, "E118", {"start": v(241.45, -25.88) * mm, "end": v(285.45, -25.88) * mm});
            skLineSegment(sketch, "E119", {"start": v(285.45, -25.88) * mm, "end": v(285.45, 13.72) * mm});
            skLineSegment(sketch, "E120", {"start": v(285.45, 13.72) * mm, "end": v(293.45, 13.72) * mm});
            skLineSegment(sketch, "E121", {"start": v(293.45, 13.72) * mm, "end": v(293.45, -25.88) * mm});
            skLineSegment(sketch, "E122", {"start": v(293.45, -25.88) * mm, "end": v(181.45, -25.88) * mm});
            skLineSegment(sketch, "E123", {"start": v(241.45, -25.88) * mm, "end": v(197.45, -25.88) * mm});
            skLineSegment(sketch, "E124", {"start": v(197.45, -25.88) * mm, "end": v(189.45, -25.88) * mm});
            skLineSegment(sketch, "E125", {"start": v(189.45, -25.88) * mm, "end": v(189.45, 13.72) * mm});
            skLineSegment(sketch, "E126", {"start": v(189.45, 13.72) * mm, "end": v(197.45, 13.72) * mm});
            skLineSegment(sketch, "E127", {"start": v(197.45, 13.72) * mm, "end": v(197.45, -25.88) * mm});
            skLineSegment(sketch, "E128", {"start": v(197.45, -17.88) * mm, "end": v(197.45, -25.88) * mm});
            skLineSegment(sketch, "E129", {"start": v(197.45, -17.88) * mm, "end": v(285.45, -17.88) * mm});
            skSolve(sketch);
        }
        {
            var Q0;
            Q0 = qSketchRegion(id + "F17", true);
            extrude(context, id + "F18", {"entities" : qUnion([Q0]), "operationType" : NewBodyOperationType.ADD, "depth" : 70 * mm, "offsetDistance" : 25 * mm});
        }
        {
            var Q0;
            Q0=makeQuery(id+"F18.opExtrude","CAP_FACE",FACE,{"disambiguationData":[OSD([sQuery(id+"F17.wireOp",EDGE,"E119"),sQuery(id+"F17.wireOp",EDGE,"E120"),sQuery(id+"F17.wireOp",EDGE,"E121"),sQuery(id+"F17.wireOp",EDGE,"E122"),sQuery(id+"F17.wireOp",EDGE,"E123"),sQuery(id+"F17.wireOp",EDGE,"E124"),sQuery(id+"F17.wireOp",EDGE,"E125"),sQuery(id+"F17.wireOp",EDGE,"E126"),sQuery(id+"F17.wireOp",EDGE,"E127"),sQuery(id+"F17.wireOp",EDGE,"E129")])],"isStart":false});
            var sketch = newSketch(context, id + "F19", { "sketchPlane" : qUnion([Q0])});
            skLineSegment(sketch, "E130", {"start": v(197.45, -17.88) * mm, "end": v(197.45, -25.88) * mm});
            skLineSegment(sketch, "E131", {"start": v(197.45, -25.88) * mm, "end": v(285.45, -25.88) * mm});
            skLineSegment(sketch, "E132", {"start": v(285.45, -25.88) * mm, "end": v(285.45, -17.88) * mm});
            skLineSegment(sketch, "E133", {"start": v(285.45, -17.88) * mm, "end": v(197.45, -17.88) * mm});
            skSolve(sketch);
        }
        {
            var Q0;
            Q0 = qSketchRegion(id + "F19", true);
            extrude(context, id + "F20", {"entities" : qUnion([Q0]), "operationType" : NewBodyOperationType.REMOVE, "oppositeDirection" : true, "depth" : 20 * mm, "offsetDistance" : 25 * mm});
        }
    });
